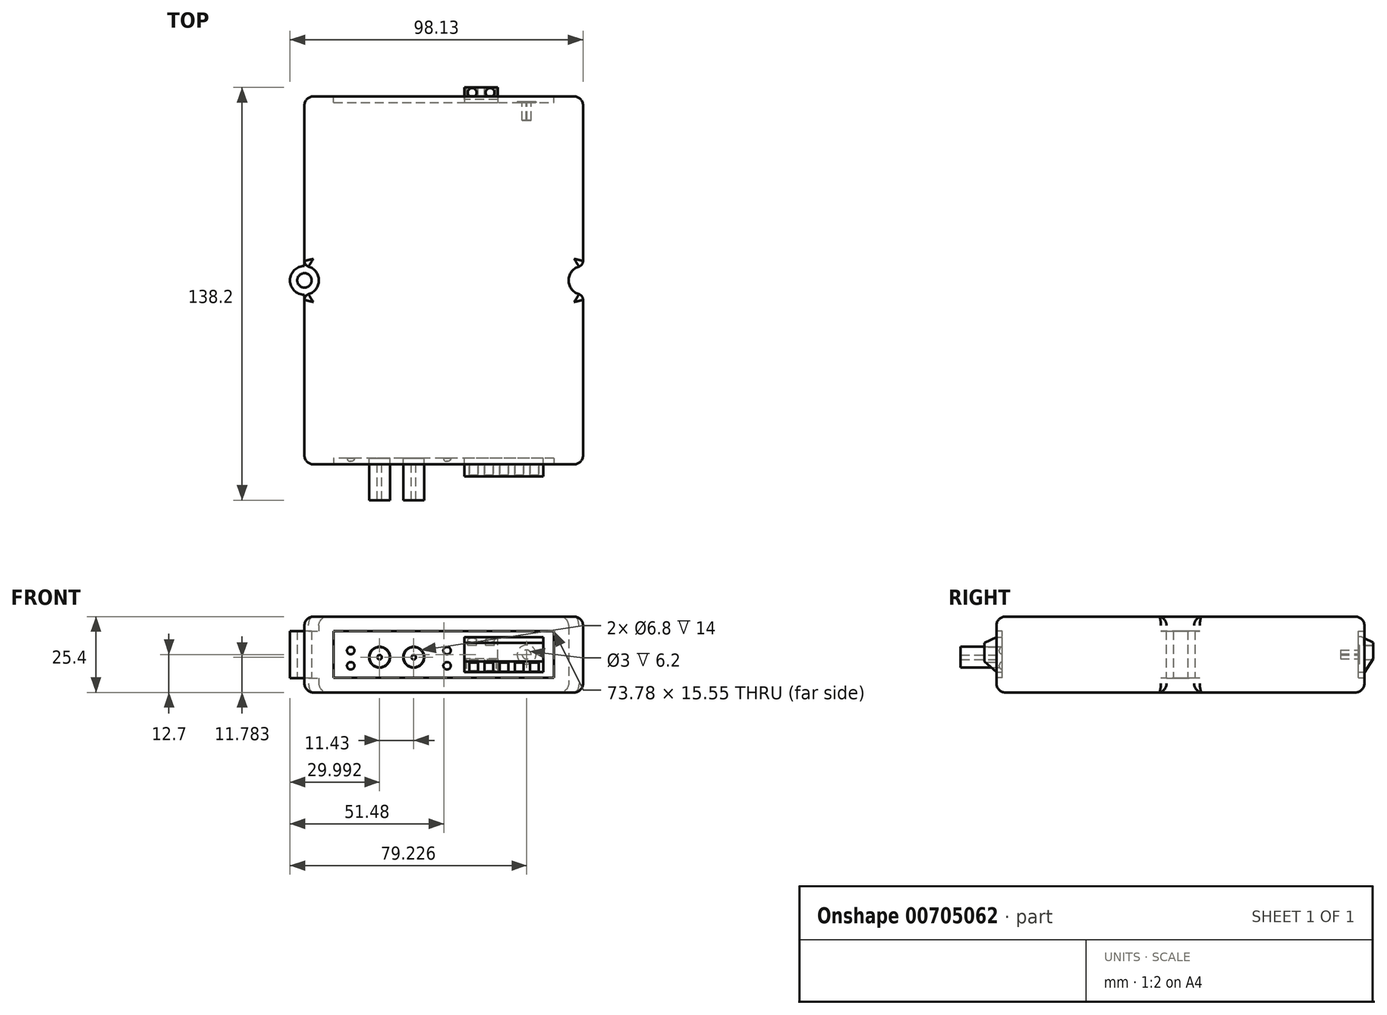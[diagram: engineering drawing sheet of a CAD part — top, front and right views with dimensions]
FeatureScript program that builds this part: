
annotation { "Feature Type Name" : "Feature", "Feature Type Description" : "" }
export const myFeature = defineFeature(function(context is Context, id is Id, definition is map)
    precondition{}
    {
        {
            var Q0;
            Q0=qCreatedBy(makeId("Top.planeOp"),FACE);
            var sketch = newSketch(context, id + "F0", { "sketchPlane" : qUnion([Q0])});
            skLineSegment(sketch, "E0.bottom", {"start": v(46.65, -61.6) * mm, "end": v(-46.65, -61.6) * mm});
            skLineSegment(sketch, "E0.top", {"start": v(46.65, 61.6) * mm, "end": v(-46.65, 61.6) * mm});
            skLineSegment(sketch, "E0.left", {"start": v(46.65, -61.6) * mm, "end": v(46.65, 61.6) * mm});
            skLineSegment(sketch, "E0.right", {"start": v(-46.65, -61.6) * mm, "end": v(-46.65, 61.6) * mm});
            skPoint(sketch, "E0.middle", {"position": v(0, 0) * mm});
            skCircle(sketch, "E1", {"center": v(-46.65, 0) * mm, "radius": 2.41 * mm});
            skCircle(sketch, "E2", {"center": v(46.65, 0) * mm, "radius": 2.41 * mm});
            skCircle(sketch, "E3", {"center": v(-46.65, 0) * mm, "radius": 4.83 * mm});
            skCircle(sketch, "E4", {"center": v(46.65, 0) * mm, "radius": 4.83 * mm});
            skSolve(sketch);
        }
        {
            var Q0;
            {var subQ1=sQuery(id+"F0.wireOp",EDGE,"E0.bottom");Q0=makeQuery(id+"F0.imprint","IMPRINT",FACE,{"disambiguationData":[TD([[makeQuery(id+"F0.imprint","IMPRINT",EDGE,{"derivedFrom":subQ1}),-1.0]])]});}
            extrude(context, id + "F1", {"entities" : qUnion([Q0]), "endBound" : BoundingType.SYMMETRIC, "depth" : 25.4 * mm, "offsetDistance" : 25 * mm});
        }
        {
            var Q0;
            {var subQ0=sQuery(id+"F0.wireOp",EDGE,"E3");var subQ1=sQuery(id+"F0.wireOp",EDGE,"E0.right");var subQ2=makeQuery(id+"F0.imprint","INTERSECT",VERTEX,{"disambiguationData":[OD(0.0)],"derivedFrom":[subQ1,subQ0]});Q0=makeQuery(id+"F0.imprint","IMPRINT",FACE,{"disambiguationData":[TD([[makeQuery(id+"F0.imprint","IMPRINT",EDGE,{"disambiguationData":[TD([[subQ2,-1.0]])],"derivedFrom":subQ1}),1.0]])]});}
            var Q1;
            {var subQ0=sQuery(id+"F0.wireOp",EDGE,"E4");var subQ1=sQuery(id+"F0.wireOp",EDGE,"E0.left");var subQ2=makeQuery(id+"F0.imprint","INTERSECT",VERTEX,{"disambiguationData":[OD(0.0)],"derivedFrom":[subQ1,subQ0]});Q1=makeQuery(id+"F0.imprint","IMPRINT",FACE,{"disambiguationData":[TD([[makeQuery(id+"F0.imprint","IMPRINT",EDGE,{"disambiguationData":[TD([[subQ2,-1.0]])],"derivedFrom":subQ1}),-1.0]])]});}
            var Q2;
            {var subQ0=sQuery(id+"F0.wireOp",EDGE,"E3");var subQ1=sQuery(id+"F0.wireOp",EDGE,"E0.right");var subQ2=makeQuery(id+"F0.imprint","INTERSECT",VERTEX,{"disambiguationData":[OD(0.0)],"derivedFrom":[subQ1,subQ0]});Q2=makeQuery(id+"F0.imprint","IMPRINT",FACE,{"disambiguationData":[TD([[makeQuery(id+"F0.imprint","IMPRINT",EDGE,{"disambiguationData":[TD([[subQ2,-1.0]])],"derivedFrom":subQ1}),-1.0]])]});}
            var Q3;
            {var subQ0=sQuery(id+"F0.wireOp",EDGE,"E4");var subQ1=sQuery(id+"F0.wireOp",EDGE,"E0.left");var subQ2=makeQuery(id+"F0.imprint","INTERSECT",VERTEX,{"disambiguationData":[OD(0.0)],"derivedFrom":[subQ1,subQ0]});Q3=makeQuery(id+"F0.imprint","IMPRINT",FACE,{"disambiguationData":[TD([[makeQuery(id+"F0.imprint","IMPRINT",EDGE,{"disambiguationData":[TD([[subQ2,-1.0]])],"derivedFrom":subQ1}),1.0]])]});}
            extrude(context, id + "F2", {"entities" : qUnion([Q0, Q1, Q2, Q3]), "operationType" : NewBodyOperationType.ADD, "endBound" : BoundingType.SYMMETRIC, "depth" : 15.72 * mm, "offsetDistance" : 25 * mm});
        }
        {
            var Q0;
            Q0=makeQuery(id+"F1.opExtrude","CAP_FACE",FACE,{"disambiguationData":[OSD([sQuery(id+"F0.wireOp",EDGE,"E0.bottom"),sQuery(id+"F0.wireOp",EDGE,"E0.top"),sQuery(id+"F0.wireOp",EDGE,"E0.left"),sQuery(id+"F0.wireOp",EDGE,"E0.right"),sQuery(id+"F0.wireOp",EDGE,"E3"),sQuery(id+"F0.wireOp",EDGE,"E4")])],"isStart":false});
            var Q1;
            Q1=makeQuery(id+"F1.opExtrude","CAP_FACE",FACE,{"disambiguationData":[OSD([sQuery(id+"F0.wireOp",EDGE,"E0.bottom"),sQuery(id+"F0.wireOp",EDGE,"E0.top"),sQuery(id+"F0.wireOp",EDGE,"E0.left"),sQuery(id+"F0.wireOp",EDGE,"E0.right"),sQuery(id+"F0.wireOp",EDGE,"E3"),sQuery(id+"F0.wireOp",EDGE,"E4")])],"isStart":true});
            var Q2;
            Q2=makeQuery(id+"F1.opExtrude","SWEPT_EDGE",EDGE,{"disambiguationData":[OSD([sQuery(id+"F0.wireOp",EDGE,"E0.bottom"),sQuery(id+"F0.wireOp",EDGE,"E0.left")])]});
            var Q3;
            Q3=makeQuery(id+"F1.opExtrude","SWEPT_EDGE",EDGE,{"disambiguationData":[OSD([sQuery(id+"F0.wireOp",EDGE,"E0.bottom"),sQuery(id+"F0.wireOp",EDGE,"E0.right")])]});
            var Q4;
            Q4=makeQuery(id+"F1.opExtrude","SWEPT_EDGE",EDGE,{"disambiguationData":[OSD([sQuery(id+"F0.wireOp",EDGE,"E0.top"),sQuery(id+"F0.wireOp",EDGE,"E0.right")])]});
            var Q5;
            Q5=makeQuery(id+"F1.opExtrude","SWEPT_EDGE",EDGE,{"disambiguationData":[OSD([sQuery(id+"F0.wireOp",EDGE,"E0.top"),sQuery(id+"F0.wireOp",EDGE,"E0.left")])]});
            fillet(context, id + "F3", {"entities" : qUnion([Q0, Q1, Q2, Q3, Q4, Q5]), "radius" : 3 * mm, "tangentPropagation" : true, "allowEdgeOverflow" : false});
        }
        {
            var Q0;
            {var subQ0=sQuery(id+"F0.wireOp",EDGE,"E0.right");var subQ1=sQuery(id+"F0.wireOp",EDGE,"E3");var subQ2=makeQuery(id+"F0.imprint","INTERSECT",VERTEX,{"disambiguationData":[OD(0.0)],"derivedFrom":[subQ0,subQ1]});Q0=makeQuery(id+"F2.boolean.opBoolean","SPLIT",EDGE,{"disambiguationData":[topologyDisambiguationEdgeConnected([makeQuery(id+"F1.opExtrude","SWEPT_FACE",FACE,{"disambiguationData":[OSD([subQ0]),TDD([makeQuery(id+"F0.imprint","IMPRINT",EDGE,{"disambiguationData":[TD([[makeQuery(id+"F0.imprint","INTERSECT",VERTEX,{"derivedFrom":[sQuery(id+"F0.wireOp",EDGE,"E0.bottom"),subQ0]}),-1.0]])],"derivedFrom":subQ0})])]}),makeQuery(id+"F2.opExtrude","SWEPT_FACE",FACE,{"disambiguationData":[OSD([subQ1])]})])],"derivedFrom":makeQuery(id+"F1.opExtrude","SWEPT_EDGE",EDGE,{"disambiguationData":[OSD([subQ0,subQ1]),TDD([subQ2])]})});}
            var Q1;
            {var subQ0=sQuery(id+"F0.wireOp",EDGE,"E0.right");var subQ1=sQuery(id+"F0.wireOp",EDGE,"E3");var subQ2=makeQuery(id+"F0.imprint","INTERSECT",VERTEX,{"disambiguationData":[OD(1.0)],"derivedFrom":[subQ0,subQ1]});Q1=makeQuery(id+"F2.boolean.opBoolean","SPLIT",EDGE,{"disambiguationData":[topologyDisambiguationEdgeConnected([makeQuery(id+"F1.opExtrude","SWEPT_FACE",FACE,{"disambiguationData":[OSD([subQ0]),TDD([makeQuery(id+"F0.imprint","IMPRINT",EDGE,{"disambiguationData":[TD([[makeQuery(id+"F0.imprint","INTERSECT",VERTEX,{"derivedFrom":[sQuery(id+"F0.wireOp",EDGE,"E0.top"),subQ0]}),1.0]])],"derivedFrom":subQ0})])]}),makeQuery(id+"F2.opExtrude","SWEPT_FACE",FACE,{"disambiguationData":[OSD([subQ1])]})])],"derivedFrom":makeQuery(id+"F1.opExtrude","SWEPT_EDGE",EDGE,{"disambiguationData":[OSD([subQ0,subQ1]),TDD([subQ2])]})});}
            var Q2;
            {var subQ0=sQuery(id+"F0.wireOp",EDGE,"E0.left");var subQ1=sQuery(id+"F0.wireOp",EDGE,"E4");var subQ2=makeQuery(id+"F0.imprint","INTERSECT",VERTEX,{"disambiguationData":[OD(0.0)],"derivedFrom":[subQ0,subQ1]});Q2=makeQuery(id+"F2.boolean.opBoolean","SPLIT",EDGE,{"disambiguationData":[topologyDisambiguationEdgeConnected([makeQuery(id+"F1.opExtrude","SWEPT_FACE",FACE,{"disambiguationData":[OSD([subQ0]),TDD([makeQuery(id+"F0.imprint","IMPRINT",EDGE,{"disambiguationData":[TD([[makeQuery(id+"F0.imprint","INTERSECT",VERTEX,{"derivedFrom":[sQuery(id+"F0.wireOp",EDGE,"E0.bottom"),subQ0]}),-1.0]])],"derivedFrom":subQ0})])]}),makeQuery(id+"F2.opExtrude","SWEPT_FACE",FACE,{"disambiguationData":[OSD([subQ1])]})])],"derivedFrom":makeQuery(id+"F1.opExtrude","SWEPT_EDGE",EDGE,{"disambiguationData":[OSD([subQ0,subQ1]),TDD([subQ2])]})});}
            var Q3;
            {var subQ0=sQuery(id+"F0.wireOp",EDGE,"E0.left");var subQ1=sQuery(id+"F0.wireOp",EDGE,"E4");var subQ2=makeQuery(id+"F0.imprint","INTERSECT",VERTEX,{"disambiguationData":[OD(1.0)],"derivedFrom":[subQ0,subQ1]});Q3=makeQuery(id+"F2.boolean.opBoolean","SPLIT",EDGE,{"disambiguationData":[topologyDisambiguationEdgeConnected([makeQuery(id+"F1.opExtrude","SWEPT_FACE",FACE,{"disambiguationData":[OSD([subQ0]),TDD([makeQuery(id+"F0.imprint","IMPRINT",EDGE,{"disambiguationData":[TD([[makeQuery(id+"F0.imprint","INTERSECT",VERTEX,{"derivedFrom":[sQuery(id+"F0.wireOp",EDGE,"E0.top"),subQ0]}),1.0]])],"derivedFrom":subQ0})])]}),makeQuery(id+"F2.opExtrude","SWEPT_FACE",FACE,{"disambiguationData":[OSD([subQ1])]})])],"derivedFrom":makeQuery(id+"F1.opExtrude","SWEPT_EDGE",EDGE,{"disambiguationData":[OSD([subQ0,subQ1]),TDD([subQ2])]})});}
            fillet(context, id + "F4", {"entities" : qUnion([Q0, Q1, Q2, Q3]), "radius" : 2 * mm, "tangentPropagation" : true, "allowEdgeOverflow" : false});
        }
        {
            var Q0;
            Q0=makeQuery(id+"F1.opExtrude","SWEPT_FACE",FACE,{"disambiguationData":[OSD([sQuery(id+"F0.wireOp",EDGE,"E0.bottom")])]});
            var sketch = newSketch(context, id + "F5", { "sketchPlane" : qUnion([Q0])});
            skLineSegment(sketch, "E5.bottom", {"start": v(36.9, -7.77) * mm, "end": v(-36.9, -7.78) * mm});
            skLineSegment(sketch, "E5.top", {"start": v(36.9, 7.78) * mm, "end": v(-36.9, 7.77) * mm});
            skLineSegment(sketch, "E5.left", {"start": v(36.9, -7.77) * mm, "end": v(36.9, 7.78) * mm});
            skLineSegment(sketch, "E5.right", {"start": v(-36.9, -7.78) * mm, "end": v(-36.9, 7.77) * mm});
            skPoint(sketch, "E5.middle", {"position": v(0, 0) * mm});
            skSolve(sketch);
        }
        {
            var Q0;
            Q0 = qSketchRegion(id + "F5", true);
            extrude(context, id + "F6", {"entities" : qUnion([Q0]), "operationType" : NewBodyOperationType.REMOVE, "oppositeDirection" : true, "depth" : 2 * mm, "offsetDistance" : 25 * mm});
        }
        {
            var Q0;
            Q0=makeQuery(id+"F1.opExtrude","SWEPT_FACE",FACE,{"disambiguationData":[OSD([sQuery(id+"F0.wireOp",EDGE,"E0.top")])]});
            var sketch = newSketch(context, id + "F7", { "sketchPlane" : qUnion([Q0])});
            skLineSegment(sketch, "E6.bottom", {"start": v(36.9, -7.77) * mm, "end": v(-36.9, -7.78) * mm});
            skLineSegment(sketch, "E6.top", {"start": v(36.9, 7.78) * mm, "end": v(-36.9, 7.77) * mm});
            skLineSegment(sketch, "E6.left", {"start": v(36.9, -7.77) * mm, "end": v(36.9, 7.78) * mm});
            skLineSegment(sketch, "E6.right", {"start": v(-36.9, -7.78) * mm, "end": v(-36.9, 7.77) * mm});
            skPoint(sketch, "E6.middle", {"position": v(0, 0) * mm});
            skSolve(sketch);
        }
        {
            var Q0;
            Q0 = qSketchRegion(id + "F7", true);
            extrude(context, id + "F8", {"entities" : qUnion([Q0]), "operationType" : NewBodyOperationType.REMOVE, "oppositeDirection" : true, "depth" : 2 * mm, "offsetDistance" : 25 * mm});
        }
        {
            var Q0;
            Q0=makeQuery(id+"F8.boolean.opBoolean","COPY",FACE,{"derivedFrom":makeQuery(id+"F8.opExtrude","CAP_FACE",FACE,{"disambiguationData":[OSD([sQuery(id+"F7.wireOp",EDGE,"E6.bottom"),sQuery(id+"F7.wireOp",EDGE,"E6.top"),sQuery(id+"F7.wireOp",EDGE,"E6.left"),sQuery(id+"F7.wireOp",EDGE,"E6.right")])],"isStart":false})});
            var sketch = newSketch(context, id + "F9", { "sketchPlane" : qUnion([Q0])});
            skCircle(sketch, "E7", {"center": v(-27.75, 0) * mm, "radius": 1.5 * mm});
            skCircle(sketch, "E8", {"center": v(-27.75, 0) * mm, "radius": 3.17 * mm});
            skLineSegment(sketch, "E9.bottom", {"start": v(-6.92, -5.97) * mm, "end": v(-18.1, -5.97) * mm});
            skLineSegment(sketch, "E9.top", {"start": v(-6.92, 5.97) * mm, "end": v(-18.1, 5.97) * mm});
            skLineSegment(sketch, "E9.left", {"start": v(-6.92, -5.97) * mm, "end": v(-6.92, 5.97) * mm});
            skLineSegment(sketch, "E9.right", {"start": v(-18.1, -5.97) * mm, "end": v(-18.1, 5.97) * mm});
            skPoint(sketch, "E9.middle", {"position": v(-12.5, 0) * mm});
            skCircle(sketch, "E10", {"center": v(-27.75, 0) * mm, "radius": 0.15 * mm});
            skSolve(sketch);
        }
        {
            var Q0;
            Q0=makeQuery(id+"F9.imprint","IMPRINT",FACE,{"disambiguationData":[TD([[makeQuery(id+"F9.imprint","IMPRINT",EDGE,{"derivedFrom":sQuery(id+"F9.wireOp",EDGE,"E9.bottom")}),-1.0]])]});
            extrude(context, id + "F10", {"entities" : qUnion([Q0]), "depth" : 5 * mm, "offsetDistance" : 25 * mm});
        }
        {
            var Q0;
            Q0=makeQuery(id+"F10.opExtrude","CAP_EDGE",EDGE,{"disambiguationData":[OSD([sQuery(id+"F9.wireOp",EDGE,"E9.top")])],"isStart":false});
            chamfer(context, id + "F11", {"entities" : qUnion([Q0]), "chamferType" : ChamferType.TWO_OFFSETS, "width1" : 2 * mm, "oppositeDirection" : false, "width2" : 4 * mm, "tangentPropagation" : true});
        }
        {
            var Q0;
            Q0=makeQuery(id+"F10.opExtrude","CAP_EDGE",EDGE,{"disambiguationData":[OSD([sQuery(id+"F9.wireOp",EDGE,"E9.bottom")])],"isStart":false});
            chamfer(context, id + "F12", {"entities" : qUnion([Q0]), "chamferType" : ChamferType.TWO_OFFSETS, "width1" : 3 * mm, "oppositeDirection" : false, "width2" : 4.5 * mm, "tangentPropagation" : true});
        }
        {
            var Q0;
            Q0=makeQuery(id+"F10.opExtrude","SWEPT_FACE",FACE,{"disambiguationData":[OSD([sQuery(id+"F9.wireOp",EDGE,"E9.top")])]});
            var sketch = newSketch(context, id + "F13", { "sketchPlane" : qUnion([Q0])});
            skCircle(sketch, "E11", {"center": v(15.5, 62.93) * mm, "radius": 1.5 * mm});
            skCircle(sketch, "E12", {"center": v(9.5, 62.93) * mm, "radius": 1.5 * mm});
            skSolve(sketch);
        }
        {
            var Q0;
            Q0 = qSketchRegion(id + "F13", true);
            extrude(context, id + "F14", {"entities" : qUnion([Q0]), "operationType" : NewBodyOperationType.REMOVE, "oppositeDirection" : true, "depth" : 3 * mm, "offsetDistance" : 25 * mm});
        }
        {
            var Q0;
            Q0=makeQuery(id+"F6.boolean.opBoolean","COPY",FACE,{"derivedFrom":makeQuery(id+"F6.opExtrude","CAP_FACE",FACE,{"disambiguationData":[OSD([sQuery(id+"F5.wireOp",EDGE,"E5.bottom"),sQuery(id+"F5.wireOp",EDGE,"E5.top"),sQuery(id+"F5.wireOp",EDGE,"E5.left"),sQuery(id+"F5.wireOp",EDGE,"E5.right")])],"isStart":false})});
            var sketch = newSketch(context, id + "F15", { "sketchPlane" : qUnion([Q0])});
            skLineSegment(sketch, "E13.bottom", {"start": v(33.39, -5.84) * mm, "end": v(6.97, -5.84) * mm});
            skLineSegment(sketch, "E13.top", {"start": v(33.39, 5.84) * mm, "end": v(6.97, 5.84) * mm});
            skLineSegment(sketch, "E13.left", {"start": v(33.39, -5.84) * mm, "end": v(33.39, 5.84) * mm});
            skLineSegment(sketch, "E13.right", {"start": v(6.97, -5.84) * mm, "end": v(6.97, 5.84) * mm});
            skPoint(sketch, "E13.middle", {"position": v(20.18, 0) * mm});
            skSolve(sketch);
        }
        {
            var Q0;
            Q0 = qSketchRegion(id + "F15", true);
            extrude(context, id + "F16", {"entities" : qUnion([Q0]), "depth" : 6 * mm, "offsetDistance" : 25 * mm});
        }
        {
            var Q0;
            Q0=makeQuery(id+"F16.opExtrude","CAP_EDGE",EDGE,{"disambiguationData":[OSD([sQuery(id+"F15.wireOp",EDGE,"E13.top")])],"isStart":false});
            chamfer(context, id + "F17", {"entities" : qUnion([Q0]), "chamferType" : ChamferType.TWO_OFFSETS, "width1" : 2 * mm, "oppositeDirection" : false, "width2" : 4 * mm, "tangentPropagation" : true});
        }
        {
            var Q0;
            Q0=makeQuery(id+"F16.opExtrude","CAP_EDGE",EDGE,{"disambiguationData":[OSD([sQuery(id+"F15.wireOp",EDGE,"E13.bottom")])],"isStart":false});
            chamfer(context, id + "F18", {"entities" : qUnion([Q0]), "chamferType" : ChamferType.TWO_OFFSETS, "width1" : 4 * mm, "oppositeDirection" : false, "width2" : 3.5 * mm, "tangentPropagation" : true});
        }
        {
            var Q0;
            Q0=makeQuery(id+"F10.opExtrude","CAP_FACE",FACE,{"disambiguationData":[OSD([sQuery(id+"F9.wireOp",EDGE,"E9.bottom"),sQuery(id+"F9.wireOp",EDGE,"E9.top"),sQuery(id+"F9.wireOp",EDGE,"E9.left"),sQuery(id+"F9.wireOp",EDGE,"E9.right")])],"isStart":false});
            var sketch = newSketch(context, id + "F19", { "sketchPlane" : qUnion([Q0])});
            skLineSegment(sketch, "E14.bottom", {"start": v(-13.6, -5.5) * mm, "end": v(-17.4, -5.5) * mm});
            skLineSegment(sketch, "E14.top", {"start": v(-13.6, -1.7) * mm, "end": v(-17.4, -1.7) * mm});
            skLineSegment(sketch, "E14.left", {"start": v(-13.6, -5.5) * mm, "end": v(-13.6, -1.7) * mm});
            skLineSegment(sketch, "E14.right", {"start": v(-17.4, -5.5) * mm, "end": v(-17.4, -1.7) * mm});
            skPoint(sketch, "E14.middle", {"position": v(-15.5, -3.6) * mm});
            skLineSegment(sketch, "E15.1.0.0", {"start": v(-7.6, -5.5) * mm, "end": v(-7.6, -1.7) * mm});
            skPoint(sketch, "E15.1.0.1", {"position": v(-9.5, -3.6) * mm});
            skLineSegment(sketch, "E15.1.0.2", {"start": v(-11.4, -5.5) * mm, "end": v(-11.4, -1.7) * mm});
            skLineSegment(sketch, "E15.1.0.3", {"start": v(-7.6, -1.7) * mm, "end": v(-11.4, -1.7) * mm});
            skLineSegment(sketch, "E15.1.0.4", {"start": v(-7.6, -5.5) * mm, "end": v(-11.4, -5.5) * mm});
            skLineSegment(sketch, "E15.direction1", {"start": v(-17.4, -5.5) * mm, "end": v(-11.4, -5.5) * mm, "construction": true});
            skSolve(sketch);
        }
        {
            var Q0;
            Q0 = qSketchRegion(id + "F19", true);
            extrude(context, id + "F20", {"entities" : qUnion([Q0]), "operationType" : NewBodyOperationType.REMOVE, "oppositeDirection" : true, "depth" : 3 * mm, "offsetDistance" : 25 * mm});
        }
        {
            var Q0;
            Q0=makeQuery(id+"F16.opExtrude","CAP_FACE",FACE,{"disambiguationData":[OSD([sQuery(id+"F15.wireOp",EDGE,"E13.bottom"),sQuery(id+"F15.wireOp",EDGE,"E13.top"),sQuery(id+"F15.wireOp",EDGE,"E13.left"),sQuery(id+"F15.wireOp",EDGE,"E13.right")])],"isStart":false});
            var sketch = newSketch(context, id + "F21", { "sketchPlane" : qUnion([Q0])});
            skLineSegment(sketch, "E16.bottom", {"start": v(11.52, -5.73) * mm, "end": v(8.52, -5.73) * mm});
            skLineSegment(sketch, "E16.top", {"start": v(11.52, -2.73) * mm, "end": v(8.52, -2.73) * mm});
            skLineSegment(sketch, "E16.left", {"start": v(11.52, -5.73) * mm, "end": v(11.52, -2.73) * mm});
            skLineSegment(sketch, "E16.right", {"start": v(8.52, -5.73) * mm, "end": v(8.52, -2.73) * mm});
            skPoint(sketch, "E16.middle", {"position": v(10.02, -4.23) * mm});
            skPoint(sketch, "E17.1.0.0", {"position": v(15.1, -4.23) * mm});
            skLineSegment(sketch, "E17.1.0.1", {"start": v(16.6, -5.73) * mm, "end": v(13.6, -5.73) * mm});
            skLineSegment(sketch, "E17.1.0.2", {"start": v(16.6, -2.73) * mm, "end": v(13.6, -2.73) * mm});
            skLineSegment(sketch, "E17.1.0.3", {"start": v(16.6, -5.73) * mm, "end": v(16.6, -2.73) * mm});
            skLineSegment(sketch, "E17.1.0.4", {"start": v(13.6, -5.73) * mm, "end": v(13.6, -2.73) * mm});
            skPoint(sketch, "E17.2.0.0", {"position": v(20.18, -4.23) * mm});
            skLineSegment(sketch, "E17.2.0.1", {"start": v(21.68, -5.73) * mm, "end": v(18.68, -5.73) * mm});
            skLineSegment(sketch, "E17.2.0.2", {"start": v(21.68, -2.73) * mm, "end": v(18.68, -2.73) * mm});
            skLineSegment(sketch, "E17.2.0.3", {"start": v(21.68, -5.73) * mm, "end": v(21.68, -2.73) * mm});
            skLineSegment(sketch, "E17.2.0.4", {"start": v(18.68, -5.73) * mm, "end": v(18.68, -2.73) * mm});
            skPoint(sketch, "E17.3.0.0", {"position": v(25.26, -4.23) * mm});
            skLineSegment(sketch, "E17.3.0.1", {"start": v(26.76, -5.73) * mm, "end": v(23.76, -5.73) * mm});
            skLineSegment(sketch, "E17.3.0.2", {"start": v(26.76, -2.73) * mm, "end": v(23.76, -2.73) * mm});
            skLineSegment(sketch, "E17.3.0.3", {"start": v(26.76, -5.73) * mm, "end": v(26.76, -2.73) * mm});
            skLineSegment(sketch, "E17.3.0.4", {"start": v(23.76, -5.73) * mm, "end": v(23.76, -2.73) * mm});
            skPoint(sketch, "E17.4.0.0", {"position": v(30.34, -4.23) * mm});
            skLineSegment(sketch, "E17.4.0.1", {"start": v(31.84, -5.73) * mm, "end": v(28.84, -5.73) * mm});
            skLineSegment(sketch, "E17.4.0.2", {"start": v(31.84, -2.73) * mm, "end": v(28.84, -2.73) * mm});
            skLineSegment(sketch, "E17.4.0.3", {"start": v(31.84, -5.73) * mm, "end": v(31.84, -2.73) * mm});
            skLineSegment(sketch, "E17.4.0.4", {"start": v(28.84, -5.73) * mm, "end": v(28.84, -2.73) * mm});
            skLineSegment(sketch, "E17.direction1", {"start": v(8.52, -5.73) * mm, "end": v(13.6, -5.73) * mm, "construction": true});
            skSolve(sketch);
        }
        {
            var Q0;
            Q0 = qSketchRegion(id + "F21", true);
            extrude(context, id + "F22", {"entities" : qUnion([Q0]), "operationType" : NewBodyOperationType.REMOVE, "oppositeDirection" : true, "depth" : 4 * mm, "offsetDistance" : 25 * mm});
        }
        {
            var Q0;
            Q0=makeQuery(id+"F9.imprint","IMPRINT",FACE,{"disambiguationData":[TD([[makeQuery(id+"F9.imprint","IMPRINT",EDGE,{"derivedFrom":sQuery(id+"F9.wireOp",EDGE,"E7")}),1.0]])]});
            extrude(context, id + "F23", {"entities" : qUnion([Q0]), "operationType" : NewBodyOperationType.REMOVE, "oppositeDirection" : true, "depth" : 6 * mm, "offsetDistance" : 25 * mm});
        }
        {
            var Q0;
            Q0=makeQuery(id+"F9.imprint","IMPRINT",FACE,{"disambiguationData":[TD([[makeQuery(id+"F9.imprint","IMPRINT",EDGE,{"derivedFrom":sQuery(id+"F9.wireOp",EDGE,"E7")}),-1.0]])]});
            extrude(context, id + "F24", {"entities" : qUnion([Q0]), "operationType" : NewBodyOperationType.ADD, "depth" : 0.2 * mm, "offsetDistance" : 25 * mm});
        }
        {
            var Q0;
            Q0=makeQuery(id+"F6.boolean.opBoolean","COPY",FACE,{"derivedFrom":makeQuery(id+"F6.opExtrude","CAP_FACE",FACE,{"disambiguationData":[OSD([sQuery(id+"F5.wireOp",EDGE,"E5.bottom"),sQuery(id+"F5.wireOp",EDGE,"E5.top"),sQuery(id+"F5.wireOp",EDGE,"E5.left"),sQuery(id+"F5.wireOp",EDGE,"E5.right")])],"isStart":false})});
            var sketch = newSketch(context, id + "F25", { "sketchPlane" : qUnion([Q0])});
            skCircle(sketch, "E18", {"center": v(1.12, 1.3) * mm, "radius": 1.25 * mm});
            skCircle(sketch, "E19", {"center": v(1.12, -3.78) * mm, "radius": 1.25 * mm});
            skCircle(sketch, "E20.1.0.0", {"center": v(-31.14, 1.3) * mm, "radius": 1.25 * mm});
            skCircle(sketch, "E20.1.0.1", {"center": v(-31.14, -3.78) * mm, "radius": 1.25 * mm});
            skLineSegment(sketch, "E20.direction1", {"start": v(1.12, 1.3) * mm, "end": v(-31.14, 1.3) * mm, "construction": true});
            skCircle(sketch, "E21", {"center": v(-21.49, -0.92) * mm, "radius": 3.5 * mm});
            skCircle(sketch, "E22", {"center": v(-10.06, -0.92) * mm, "radius": 3.5 * mm});
            skCircle(sketch, "E23", {"center": v(-21.49, -0.92) * mm, "radius": 0.75 * mm});
            skCircle(sketch, "E24", {"center": v(-10.06, -0.92) * mm, "radius": 0.75 * mm});
            skCircle(sketch, "E25", {"center": v(-10.06, -0.92) * mm, "radius": 3.4 * mm});
            skCircle(sketch, "E26", {"center": v(-21.49, -0.92) * mm, "radius": 3.4 * mm});
            skSolve(sketch);
        }
        {
            var Q0;
            Q0=makeQuery(id+"F25.imprint","IMPRINT",FACE,{"disambiguationData":[TD([[makeQuery(id+"F25.imprint","IMPRINT",EDGE,{"derivedFrom":sQuery(id+"F25.wireOp",EDGE,"E22")}),1.0]])]});
            var Q1;
            Q1=makeQuery(id+"F25.imprint","IMPRINT",FACE,{"disambiguationData":[TD([[makeQuery(id+"F25.imprint","IMPRINT",EDGE,{"derivedFrom":sQuery(id+"F25.wireOp",EDGE,"E21")}),1.0]])]});
            var Q2;
            Q2=makeQuery(id+"F25.imprint","IMPRINT",FACE,{"disambiguationData":[TD([[makeQuery(id+"F25.imprint","IMPRINT",EDGE,{"derivedFrom":sQuery(id+"F25.wireOp",EDGE,"E23")}),1.0]])]});
            var Q3;
            Q3=makeQuery(id+"F25.imprint","IMPRINT",FACE,{"disambiguationData":[TD([[makeQuery(id+"F25.imprint","IMPRINT",EDGE,{"derivedFrom":sQuery(id+"F25.wireOp",EDGE,"E24")}),1.0]])]});
            extrude(context, id + "F26", {"entities" : qUnion([Q0, Q1, Q2, Q3]), "operationType" : NewBodyOperationType.ADD, "depth" : 14 * mm, "offsetDistance" : 25 * mm});
        }
        {
            var Q0;
            Q0=qCreatedBy(makeId("Top.planeOp"),FACE);
            cPlane(context, id + "F27", {"entities" : qUnion([Q0]), "cplaneType" : CPlaneType.OFFSET, "offset" : 0.92 * mm, "oppositeDirection" : true, "width" : 150 * mm, "height" : 150 * mm});
        }
        {
            var Q0;
            Q0=makeQuery(id+"F25.imprint","IMPRINT",FACE,{"disambiguationData":[TD([[makeQuery(id+"F25.imprint","IMPRINT",EDGE,{"derivedFrom":sQuery(id+"F25.wireOp",EDGE,"E19")}),1.0]])]});
            var Q1;
            Q1=makeQuery(id+"F25.imprint","IMPRINT",FACE,{"disambiguationData":[TD([[makeQuery(id+"F25.imprint","IMPRINT",EDGE,{"derivedFrom":sQuery(id+"F25.wireOp",EDGE,"E18")}),1.0]])]});
            var Q2;
            Q2=makeQuery(id+"F25.imprint","IMPRINT",FACE,{"disambiguationData":[TD([[makeQuery(id+"F25.imprint","IMPRINT",EDGE,{"derivedFrom":sQuery(id+"F25.wireOp",EDGE,"E20.1.0.1")}),1.0]])]});
            var Q3;
            Q3=makeQuery(id+"F25.imprint","IMPRINT",FACE,{"disambiguationData":[TD([[makeQuery(id+"F25.imprint","IMPRINT",EDGE,{"derivedFrom":sQuery(id+"F25.wireOp",EDGE,"E20.1.0.0")}),1.0]])]});
            extrude(context, id + "F28", {"entities" : qUnion([Q0, Q1, Q2, Q3]), "operationType" : NewBodyOperationType.ADD, "depth" : 1 * mm, "offsetDistance" : 25 * mm});
        }
        {
            var Q0;
            Q0=makeQuery(id+"F28.opExtrude","CAP_FACE",FACE,{"disambiguationData":[OSD([sQuery(id+"F25.wireOp",EDGE,"E20.1.0.0")])],"isStart":false});
            var Q1;
            Q1=makeQuery(id+"F28.opExtrude","CAP_FACE",FACE,{"disambiguationData":[OSD([sQuery(id+"F25.wireOp",EDGE,"E20.1.0.1")])],"isStart":false});
            var Q2;
            Q2=makeQuery(id+"F28.opExtrude","CAP_FACE",FACE,{"disambiguationData":[OSD([sQuery(id+"F25.wireOp",EDGE,"E19")])],"isStart":false});
            var Q3;
            Q3=makeQuery(id+"F28.opExtrude","CAP_FACE",FACE,{"disambiguationData":[OSD([sQuery(id+"F25.wireOp",EDGE,"E18")])],"isStart":false});
            fillet(context, id + "F29", {"entities" : qUnion([Q0, Q1, Q2, Q3]), "radius" : 1 * mm, "tangentPropagation" : true, "allowEdgeOverflow" : false});
        }
    });
